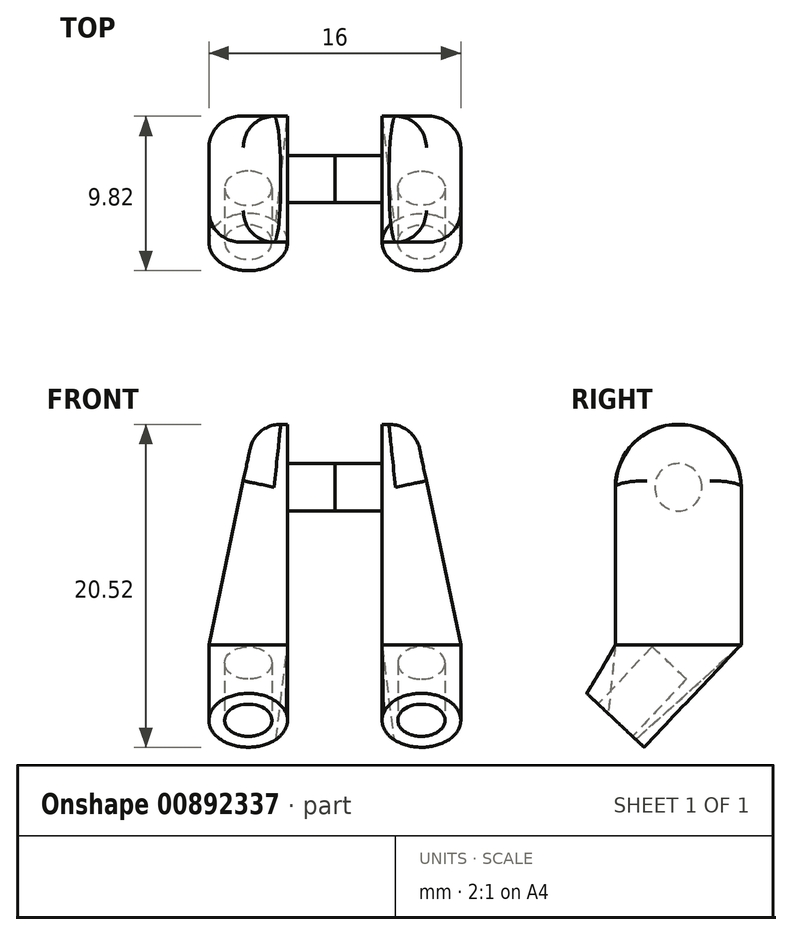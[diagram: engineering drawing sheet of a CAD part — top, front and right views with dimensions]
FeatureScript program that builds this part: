
annotation { "Feature Type Name" : "Feature", "Feature Type Description" : "" }
export const myFeature = defineFeature(function(context is Context, id is Id, definition is map)
    precondition{}
    {
        {
            var Q0;
            Q0=qCreatedBy(makeId("Right.planeOp"),FACE);
            var sketch = newSketch(context, id + "F0", { "sketchPlane" : qUnion([Q0])});
            skCircle(sketch, "E0", {"center": v(0, 0) * mm, "radius": 1.5 * mm});
            skSolve(sketch);
        }
        {
            var Q0;
            Q0 = qSketchRegion(id + "F0", true);
            extrude(context, id + "F1", {"entities" : qUnion([Q0]), "depth" : 3 * mm, "offsetDistance" : 25.4 * mm});
        }
        {
            var Q0;
            Q0=makeQuery(id+"F1.opExtrude","CAP_FACE",FACE,{"disambiguationData":[OSD([sQuery(id+"F0.wireOp",EDGE,"E0")])],"isStart":false});
            var sketch = newSketch(context, id + "F2", { "sketchPlane" : qUnion([Q0])});
            skArc(sketch, "E1", {"start": v(4, 0) * mm, "mid": v(0, 4) * mm, "end": v(-4, 0) * mm});
            skLineSegment(sketch, "E2.top", {"start": v(4, -10) * mm, "end": v(-4, -10) * mm});
            skLineSegment(sketch, "E2.left", {"start": v(4, 0) * mm, "end": v(4, -10) * mm});
            skLineSegment(sketch, "E2.right", {"start": v(-4, 0) * mm, "end": v(-4, -10) * mm});
            skPoint(sketch, "E2.middle", {"position": v(0, -5) * mm});
            skLineSegment(sketch, "E3", {"start": v(4, -10.4) * mm, "end": v(-1.95, -16.73) * mm, "construction": true});
            skLineSegment(sketch, "E4", {"start": v(-4, -10) * mm, "end": v(-6.4, -12.55) * mm, "construction": true});
            skLineSegment(sketch, "E5", {"start": v(-6.4, -12.55) * mm, "end": v(-1.95, -16.73) * mm, "construction": true});
            skLineSegment(sketch, "E6", {"start": v(-4, -14.8) * mm, "end": v(-1.55, -12.2) * mm, "construction": true});
            skSolve(sketch);
        }
        {
            var Q0;
            Q0 = qSketchRegion(id + "F2", true);
            extrude(context, id + "F3", {"entities" : qUnion([Q0]), "operationType" : NewBodyOperationType.ADD, "depth" : 5 * mm, "offsetDistance" : 25.4 * mm});
        }
        {
            var Q0;
            Q0=makeQuery(id+"F3.opExtrude","SWEPT_FACE",FACE,{"disambiguationData":[OSD([sQuery(id+"F2.wireOp",EDGE,"E2.right")])]});
            var sketch = newSketch(context, id + "F4", { "sketchPlane" : qUnion([Q0])});
            skLineSegment(sketch, "E7", {"start": v(8, -10) * mm, "end": v(4.88, 4.86) * mm});
            skLineSegment(sketch, "E8", {"start": v(4.88, 4.86) * mm, "end": v(9.76, 4.86) * mm});
            skLineSegment(sketch, "E9", {"start": v(9.76, 4.86) * mm, "end": v(8, -10) * mm});
            skSolve(sketch);
        }
        {
            var Q0;
            Q0 = qSketchRegion(id + "F4", true);
            extrude(context, id + "F5", {"entities" : qUnion([Q0]), "operationType" : NewBodyOperationType.REMOVE, "oppositeDirection" : true, "depth" : 25 * mm, "offsetDistance" : 25.4 * mm});
        }
        {
            var Q0;
            Q0=makeQuery(id+"F5.boolean.opBoolean","COPY",EDGE,{"derivedFrom":makeQuery(id+"F5.opExtrude","CAP_EDGE",EDGE,{"disambiguationData":[OSD([sQuery(id+"F4.wireOp",EDGE,"E7")])],"isStart":true})});
            var Q1;
            Q1=makeQuery(id+"F5.boolean.opBoolean","INTERSECT",EDGE,{"derivedFrom":[makeQuery(id+"F3.opExtrude","SWEPT_FACE",FACE,{"disambiguationData":[OSD([sQuery(id+"F2.wireOp",EDGE,"E1")])]}),makeQuery(id+"F5.opExtrude","SWEPT_FACE",FACE,{"disambiguationData":[OSD([sQuery(id+"F4.wireOp",EDGE,"E7")])]})]});
            fillet(context, id + "F6", {"entities" : qUnion([Q0, Q1]), "radius" : 2 * mm, "tangentPropagation" : true, "allowEdgeOverflow" : false});
        }
        {
            var Q0;
            Q0=sQuery(id+"F2.wireOp",VERTEX,"E4.end");
            var Q1;
            Q1=sQuery(id+"F2.wireOp",EDGE,"E4");
            cPlane(context, id + "F7", {"entities" : qUnion([Q0, Q1]), "cplaneType" : CPlaneType.LINE_POINT, "offset" : 25.4 * mm, "width" : 152.4 * mm, "height" : 152.4 * mm});
        }
        {
            var Q0;
            Q0=qCreatedBy(id+"F7.planeOp",FACE);
            var sketch = newSketch(context, id + "F8", { "sketchPlane" : qUnion([Q0])});
            skLineSegment(sketch, "E10", {"start": v(3, -7.22) * mm, "end": v(8.82, -7.22) * mm, "construction": true});
            skCircle(sketch, "E11", {"center": v(5.5, -7.22) * mm, "radius": 2.5 * mm});
            skSolve(sketch);
        }
        {
            var Q1;
            Q1=makeQuery(id+"F3.opExtrude","SWEPT_FACE",FACE,{"disambiguationData":[OSD([sQuery(id+"F2.wireOp",EDGE,"E2.top")])]});
            var Q2;
            Q2=makeQuery(id+"F8.imprint","IMPRINT",FACE,{"disambiguationData":[TD([[makeQuery(id+"F8.imprint","IMPRINT",EDGE,{"derivedFrom":sQuery(id+"F8.wireOp",EDGE,"E11")}),1.0]])]});
            loft(context, id + "F9", {"operationType" : NewBodyOperationType.ADD, "sheetProfilesArray" : [{ "sheetProfileEntities" : qUnion([Q1]) }, { "sheetProfileEntities" : qUnion([Q2]) }]});
        }
        {
            var Q0;
            Q0=qCreatedBy(id+"F7.planeOp",FACE);
            var sketch = newSketch(context, id + "F10", { "sketchPlane" : qUnion([Q0])});
            skCircle(sketch, "E12", {"center": v(5.5, -7.22) * mm, "radius": 1.5 * mm});
            skSolve(sketch);
        }
        {
            var Q0;
            Q0 = qSketchRegion(id + "F10", true);
            extrude(context, id + "F11", {"entities" : qUnion([Q0]), "operationType" : NewBodyOperationType.REMOVE, "oppositeDirection" : true, "depth" : 5 * mm, "offsetDistance" : 25.4 * mm});
        }
        {
            var Q0;
            Q0=makeQuery(id+"F1.opExtrude","SWEPT_BODY",BODY,{"disambiguationData":[OSD([sQuery(id+"F0.wireOp",EDGE,"E0")])]});
            var Q1;
            Q1=makeQuery(id+"F1.opExtrude","CAP_FACE",FACE,{"disambiguationData":[OSD([sQuery(id+"F0.wireOp",EDGE,"E0")])],"isStart":true});
            mirror(context, id + "F12", {"entities" : qUnion([Q0]), "mirrorPlane" : qUnion([Q1])});
        }
    });
